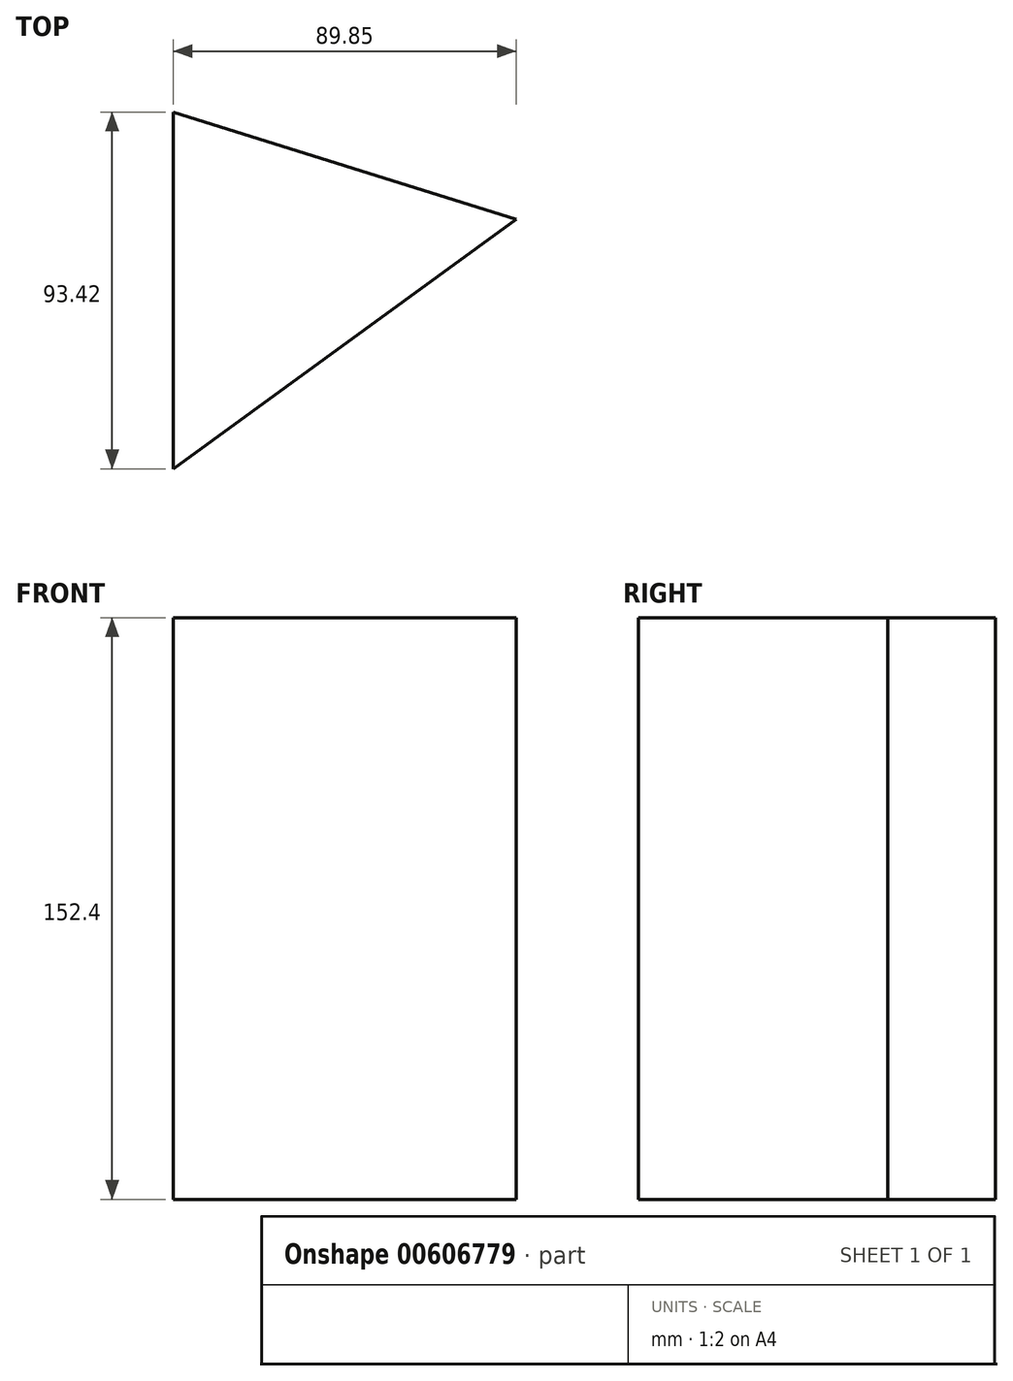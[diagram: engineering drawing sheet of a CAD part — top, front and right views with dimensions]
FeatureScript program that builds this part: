
annotation { "Feature Type Name" : "Feature", "Feature Type Description" : "" }
export const myFeature = defineFeature(function(context is Context, id is Id, definition is map)
    precondition{}
    {
        {
            var Q0;
            Q0=qCreatedBy(makeId("Top.planeOp"),FACE);
            var sketch = newSketch(context, id + "F0", { "sketchPlane" : qUnion([Q0])});
            skLineSegment(sketch, "E0", {"start": v(-42.53, -45.36) * mm, "end": v(-42.53, 48.06) * mm});
            skLineSegment(sketch, "E1", {"start": v(-42.53, 48.06) * mm, "end": v(47.32, 19.93) * mm});
            skLineSegment(sketch, "E2", {"start": v(47.32, 19.93) * mm, "end": v(-42.53, -45.36) * mm});
            skSolve(sketch);
        }
        {
            var Q0;
            Q0 = qSketchRegion(id + "F0", true);
            extrude(context, id + "F1", {"entities" : qUnion([Q0]), "oppositeDirection" : true, "depth" : 152.4 * mm, "offsetDistance" : 25.4 * mm});
        }
    });
